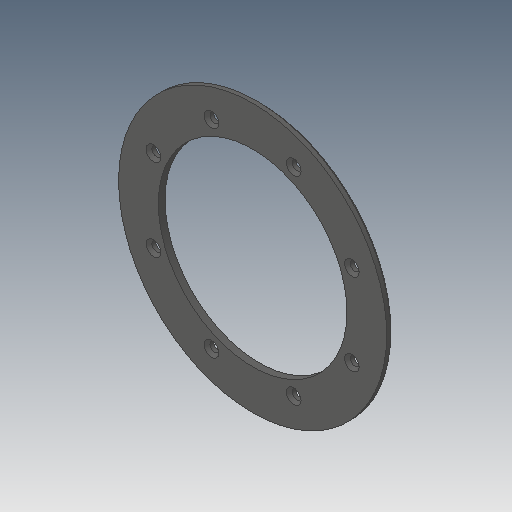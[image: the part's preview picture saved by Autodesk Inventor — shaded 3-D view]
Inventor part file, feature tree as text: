
AUTODESK INVENTOR PART (.ipt)
format: ipt  version: 2019.4 (Build 234330000, 330)  size: 124,928 bytes
history: native  units: mm
features: other x5, reference x3, sketch x2, extrude x1, chamfer x1, hole x1
ambient origin geometry x8: Origin, YZ Plane, XZ Plane, XY Plane, X Axis, Y Axis, Z Axis, Center Point
bodies: Body1 (feature_tree)
feature tree (13):
  other  "ソリッド1"
  extrude  "押し出し1"  Depth=1.0mm TaperAngle=0.0deg
  chamfer  "面取り1"  Distance=0.05mm
  hole  "穴1"  [1 undecoded]
  sketch  "スケッチ1"
  reference  "参照1"
  reference  "参照2"
  sketch  "スケッチ2"
  reference  "参照3"
  parser-record x1  (decoder bookkeeping rows leaked as tree rows — omitted from the tree; the rows remain in map.json)
  other  "COXA_PITCH_DRIVER_PULLEY.iam"
  other  "UPPER_TIMING_PULLEY_COVER_OUTER:1"
  other  "UPPER_TIMING_PULLEY_P40:1"
note: 1 required parameter value undecoded (feature->parameter linkage not recoverable at this tier; creation-order binding heuristic only, values carry confidence <= 0.55)
note: 1 file-system path scrubbed to <path> (originals preserved in map.json)
